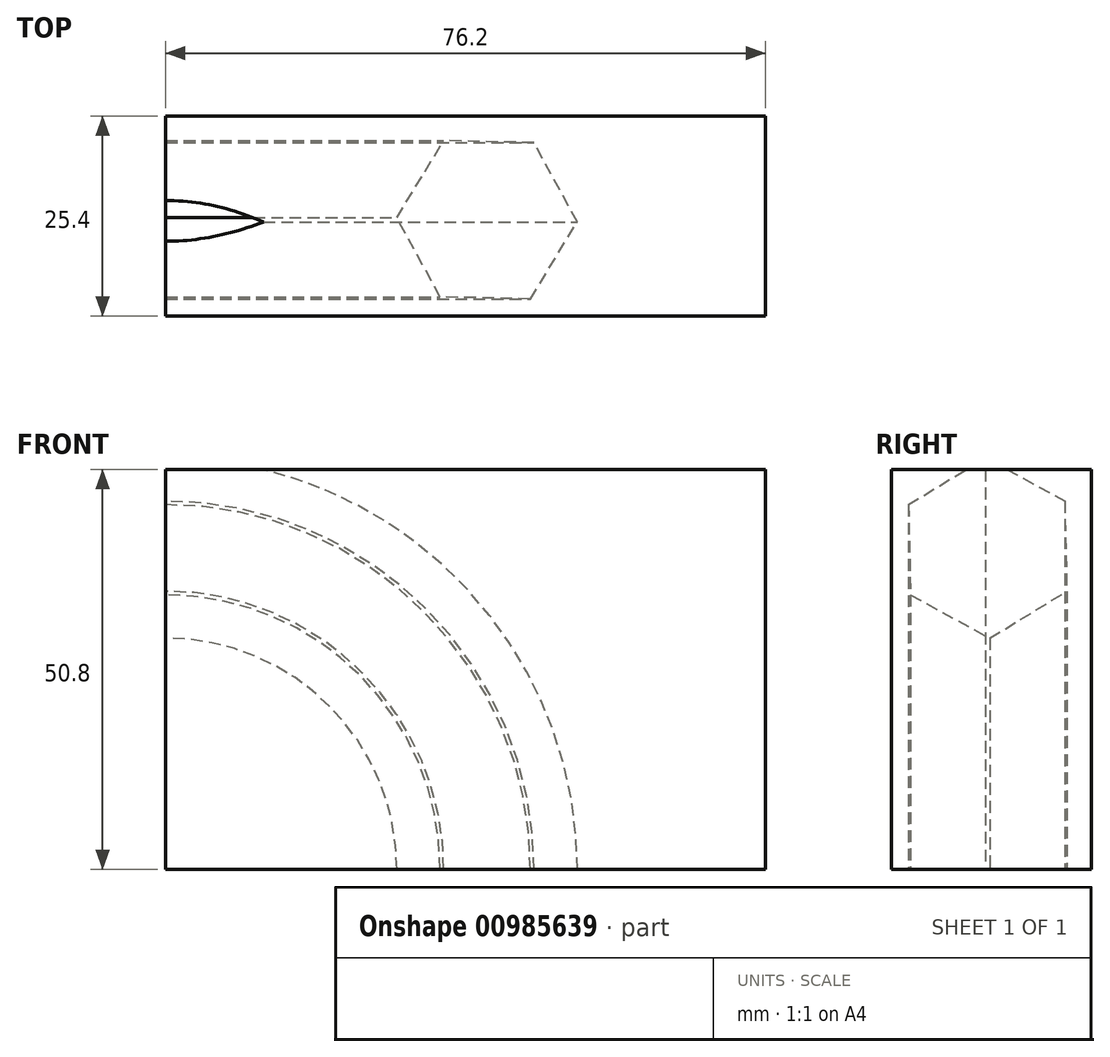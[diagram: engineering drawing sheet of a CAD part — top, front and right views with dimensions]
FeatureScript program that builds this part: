
annotation { "Feature Type Name" : "Feature", "Feature Type Description" : "" }
export const myFeature = defineFeature(function(context is Context, id is Id, definition is map)
    precondition{}
    {
        {
            var Q0;
            Q0=qCreatedBy(makeId("Front.planeOp"),FACE);
            var sketch = newSketch(context, id + "F0", { "sketchPlane" : qUnion([Q0])});
            skLineSegment(sketch, "E0.bottom", {"start": v(0, 0) * mm, "end": v(76.2, 0) * mm});
            skLineSegment(sketch, "E0.top", {"start": v(0, 50.8) * mm, "end": v(76.2, 50.8) * mm});
            skLineSegment(sketch, "E0.left", {"start": v(0, 0) * mm, "end": v(0, 50.8) * mm});
            skLineSegment(sketch, "E0.right", {"start": v(76.2, 0) * mm, "end": v(76.2, 50.8) * mm});
            skSolve(sketch);
        }
        {
            var Q0;
            Q0=makeQuery(id+"F0.imprint","IMPRINT",FACE,{"disambiguationData":[TD([[makeQuery(id+"F0.imprint","IMPRINT",EDGE,{"derivedFrom":sQuery(id+"F0.wireOp",EDGE,"E0.bottom")}),1.0]])]});
            extrude(context, id + "F1", {"entities" : qUnion([Q0]), "depth" : 25.4 * mm, "offsetDistance" : 25.4 * mm});
        }
        {
            var Q0;
            Q0=qCreatedBy(makeId("Right.planeOp"),FACE);
            var sketch = newSketch(context, id + "F2", { "sketchPlane" : qUnion([Q0])});
            skCircle(sketch, "E1.cCircle", {"center": v(-13.18, 40.83) * mm, "radius": 9.93 * mm, "construction": true});
            skLineSegment(sketch, "E1.0", {"start": v(-3.12, 35.33) * mm, "end": v(-12.92, 29.37) * mm});
            skLineSegment(sketch, "E1.1", {"start": v(-12.92, 29.37) * mm, "end": v(-22.97, 34.87) * mm});
            skLineSegment(sketch, "E1.2", {"start": v(-22.97, 34.87) * mm, "end": v(-23.24, 46.33) * mm});
            skLineSegment(sketch, "E1.3", {"start": v(-23.24, 46.33) * mm, "end": v(-13.45, 52.3) * mm});
            skLineSegment(sketch, "E1.4", {"start": v(-13.45, 52.3) * mm, "end": v(-3.39, 46.8) * mm});
            skLineSegment(sketch, "E1.5", {"start": v(-3.39, 46.8) * mm, "end": v(-3.12, 35.33) * mm});
            skPoint(sketch, "E1.0.midPoint", {"position": v(-8.02, 32.35) * mm});
            skSolve(sketch);
        }
        {
            var Q0;
            Q0=makeQuery(id+"F2.imprint","IMPRINT",FACE,{"disambiguationData":[TD([[makeQuery(id+"F2.imprint","IMPRINT",EDGE,{"derivedFrom":sQuery(id+"F2.wireOp",EDGE,"E1.0")}),-1.0]])]});
            var Q1;
            Q1=makeQuery(id+"F1.opExtrude","SWEPT_EDGE",EDGE,{"disambiguationData":[OSD([sQuery(id+"F0.wireOp",EDGE,"E0.bottom"),sQuery(id+"F0.wireOp",EDGE,"E0.left")])]});
            revolve(context, id + "F3", {"operationType" : NewBodyOperationType.REMOVE, "surfaceOperationType" : NewSurfaceOperationType.NEW, "entities" : qUnion([Q0]), "axis" : qUnion([Q1]), "revolveType" : RevolveType.FULL, "oppositeDirection" : true});
        }
    });
